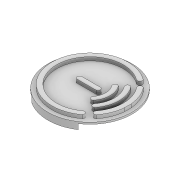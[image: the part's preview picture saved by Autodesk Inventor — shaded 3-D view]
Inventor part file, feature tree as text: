
AUTODESK INVENTOR PART (.ipt)
format: ipt  version: 2020.3 (Build 243373000, 373)  size: 190,464 bytes
history: native  units: mm
features: extrude x4, sketch x4
ambient origin geometry x8: Origin, YZ Plane, XZ Plane, XY Plane, X Axis, Y Axis, Z Axis, Center Point
bodies: Solid1 (feature_tree)
feature tree (8):
  extrude  "Extrusion1"  Depth=2.0mm
  extrude  "Extrusion2"  Depth=1.0mm TaperAngle=0.0deg
  sketch  "Sketch3"  dims[d7=60.0mm d8=40.0mm]
  extrude  "Extrusion3"  Depth=40.0mm
  extrude  "Extrusion4"  Depth=10.0mm
  sketch  "Sketch1"  dims[d0=48.0mm d2=2.0mm]
  sketch  "Sketch2"  dims[d3=4.0mm d4=0.0mm d5=1.0mm d6=0.0mm]
  sketch  "Sketch4"  dims[d10=40.0mm d11=48.0mm d12=44.0mm d13=34.0mm d14=28.0mm d15=22.0mm d16=14.0mm d17=8.0mm d18=38.074mm d19=2.65912mm d20=2.65912mm d21=2.65912mm d22=2.417382mm d23=2.417382mm d24=1.369mm d25=2.659266mm d26=1.352mm d27=1.351mm d28=2.0mm d29=0.0mm d30=10.0mm d31=0.0mm]
